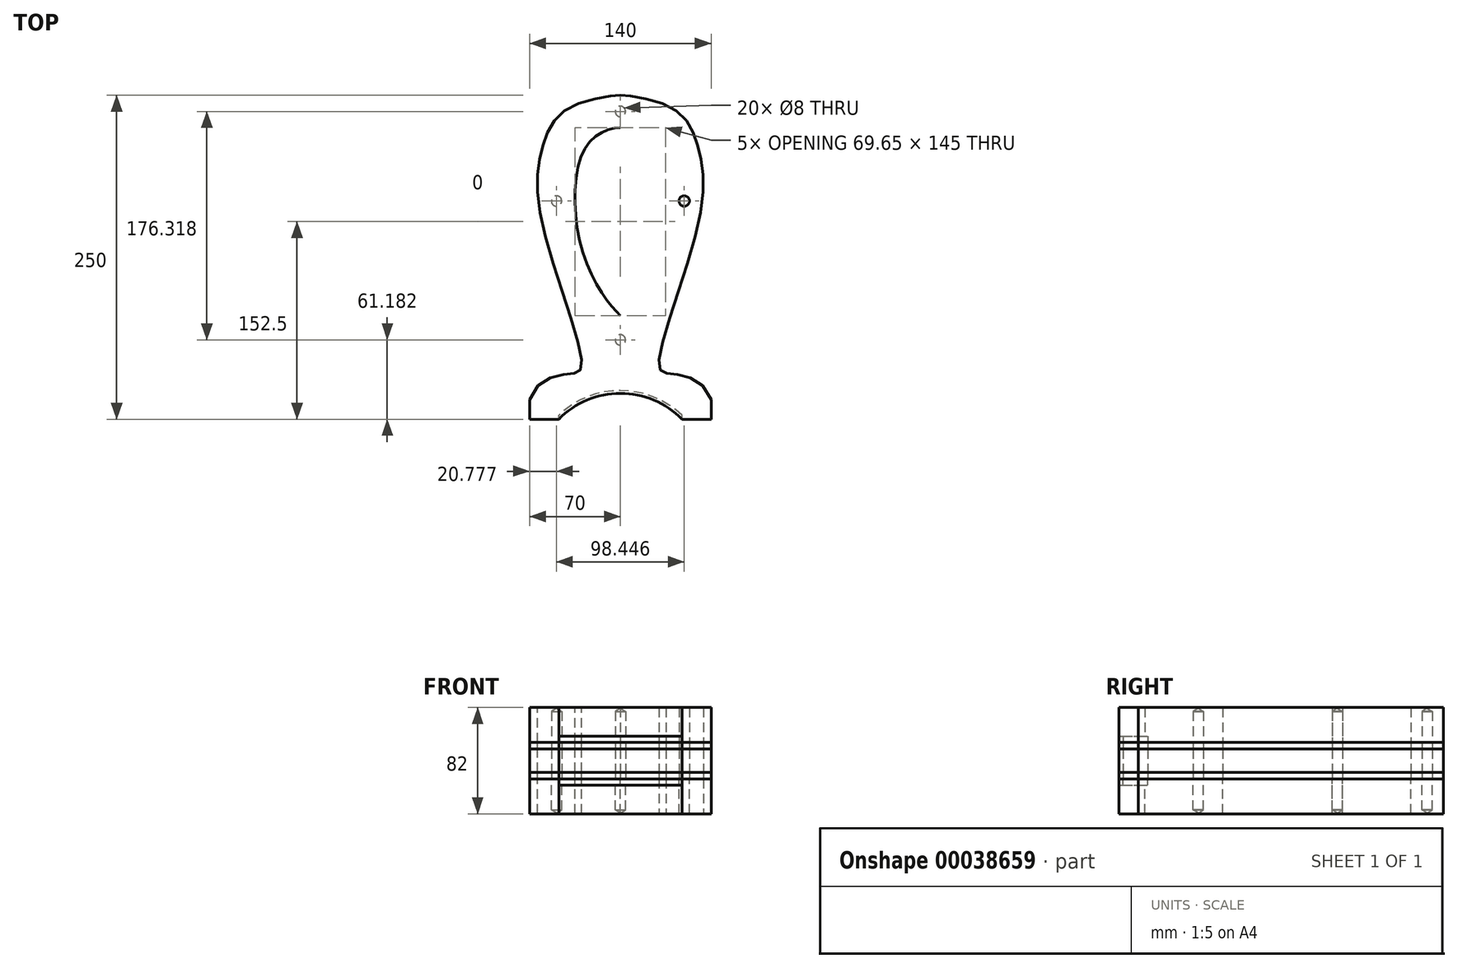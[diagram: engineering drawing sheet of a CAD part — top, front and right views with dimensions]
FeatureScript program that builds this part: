
annotation { "Feature Type Name" : "Feature", "Feature Type Description" : "" }
export const myFeature = defineFeature(function(context is Context, id is Id, definition is map)
    precondition{}
    {
        {
            assignVariable(context, id + "F0", {"name" : "WoodFrontWidth", "anyValue" : 27});
        }
        {
            assignVariable(context, id + "F1", {"name" : "WoodMiddleWidth", "anyValue" : 18});
        }
        {
            assignVariable(context, id + "F2", {"name" : "PlexiWidth", "anyValue" : 5});
        }
        {
            var Q0;
            Q0=qCreatedBy(makeId("Top.planeOp"),FACE);
            var sketch = newSketch(context, id + "F3", { "sketchPlane" : qUnion([Q0])});
            skLineSegment(sketch, "E0", {"start": v(-70, -35) * mm, "end": v(-47.5, -35) * mm});
            skArc(sketch, "E1", {"start": v(0, -15) * mm, "mid": v(-25.77, -20.2) * mm, "end": v(-47.5, -35) * mm});
            skLineSegment(sketch, "E2", {"start": v(-70, -35) * mm, "end": v(-70, -20) * mm});
            skFitSpline(sketch, "E3", {"points": [v(-70, -20) * mm, v(-40, 0) * mm, v(-30, 5) * mm, v(-60, 115) * mm, v(-60, 175) * mm, v(-40, 205) * mm, v(0, 215) * mm], "startDerivative": vector(94.53, 318.3) * mm, "endDerivative": vector(113.11, -0.2) * mm});
            skFitSpline(sketch, "E4", {"points": [v(0, 190) * mm, v(-26.56, 175) * mm, v(-27.76, 90.21) * mm, v(0, 45) * mm], "startDerivative": vector(-99.5, -1.22) * mm, "endDerivative": vector(63.74, -58) * mm});
            skArc(sketch, "E5.MirrorCS", {"start": v(0, -15) * mm, "mid": v(25.77, -20.2) * mm, "end": v(47.5, -35) * mm});
            skLineSegment(sketch, "E6.MirrorCS", {"start": v(70, -35) * mm, "end": v(70, -20) * mm});
            skLineSegment(sketch, "E7.MirrorCS", {"start": v(70, -35) * mm, "end": v(47.5, -35) * mm});
            skFitSpline(sketch, "E8.MirrorCS", {"points": [v(70, -20) * mm, v(40, 0) * mm, v(30, 5) * mm, v(60, 115) * mm, v(60, 175) * mm, v(40, 205) * mm, v(0, 215) * mm], "startDerivative": vector(-94.53, 318.3) * mm, "endDerivative": vector(-113.11, -0.2) * mm});
            skFitSpline(sketch, "E9.MirrorCS", {"points": [v(-70, -20) * mm, v(-40, 0) * mm, v(-30, 5) * mm, v(-60, 115) * mm, v(-60, 175) * mm, v(-40, 205) * mm, v(0, 215) * mm], "startDerivative": vector(94.53, 318.3) * mm, "endDerivative": vector(113.11, -0.2) * mm});
            skFitSpline(sketch, "E10.MirrorCS", {"points": [v(70, -20) * mm, v(40, 0) * mm, v(30, 5) * mm, v(60, 115) * mm, v(60, 175) * mm, v(40, 205) * mm, v(0, 215) * mm], "startDerivative": vector(-94.53, 318.3) * mm, "endDerivative": vector(-113.11, -0.2) * mm});
            skFitSpline(sketch, "E11.MirrorCS", {"points": [v(0, 190) * mm, v(26.56, 175) * mm, v(27.76, 90.21) * mm, v(0, 45) * mm], "startDerivative": vector(99.5, -1.22) * mm, "endDerivative": vector(-63.74, -58) * mm});
            skCircle(sketch, "E12", {"center": v(0, 26.18) * mm, "radius": 4 * mm});
            skCircle(sketch, "E13", {"center": v(-49.22, 133.37) * mm, "radius": 4 * mm});
            skCircle(sketch, "E14", {"center": v(0, 202.5) * mm, "radius": 4 * mm});
            skCircle(sketch, "E15.MirrorC", {"center": v(49.22, 133.37) * mm, "radius": 4 * mm});
            skLineSegment(sketch, "E16.bottom", {"start": v(-37, -26.26) * mm, "end": v(37, -26.26) * mm});
            skLineSegment(sketch, "E16.top", {"start": v(-37, -56.26) * mm, "end": v(37, -56.26) * mm});
            skLineSegment(sketch, "E16.left", {"start": v(-37, -26.26) * mm, "end": v(-37, -56.26) * mm});
            skLineSegment(sketch, "E16.right", {"start": v(37, -26.26) * mm, "end": v(37, -56.26) * mm});
            skLineSegment(sketch, "E17.bottom", {"start": v(-47.5, -56.26) * mm, "end": v(47.5, -56.26) * mm});
            skLineSegment(sketch, "E17.top", {"start": v(-47.5, -88.26) * mm, "end": v(47.5, -88.26) * mm});
            skLineSegment(sketch, "E17.left", {"start": v(-47.5, -56.26) * mm, "end": v(-47.5, -88.26) * mm});
            skLineSegment(sketch, "E17.right", {"start": v(47.5, -56.26) * mm, "end": v(47.5, -88.26) * mm});
            skLineSegment(sketch, "E18", {"start": v(-47.5, -88.26) * mm, "end": v(-70, -88.26) * mm});
            skLineSegment(sketch, "E19", {"start": v(-70, -88.26) * mm, "end": v(-70, -35) * mm});
            skLineSegment(sketch, "E20.MirrorCS", {"start": v(70, -88.26) * mm, "end": v(70, -35) * mm});
            skLineSegment(sketch, "E21.MirrorCS", {"start": v(47.5, -88.26) * mm, "end": v(70, -88.26) * mm});
            skLineSegment(sketch, "E22", {"start": v(-47.5, -35) * mm, "end": v(-47.5, -32) * mm});
            skArc(sketch, "E23", {"start": v(0, -12.87) * mm, "mid": v(-25.6, -17.83) * mm, "end": v(-47.5, -32) * mm});
            skArc(sketch, "E24.MirrorCS", {"start": v(0, -12.87) * mm, "mid": v(25.6, -17.83) * mm, "end": v(47.5, -32) * mm});
            skLineSegment(sketch, "E25.MirrorCS", {"start": v(47.5, -35) * mm, "end": v(47.5, -32) * mm});
            skSolve(sketch);
        }
        {
            var Q0;
            Q0=makeQuery(id+"F3.imprint","IMPRINT",FACE,{"disambiguationData":[TD([[makeQuery(id+"F3.imprint","IMPRINT",EDGE,{"derivedFrom":sQuery(id+"F3.wireOp",EDGE,"E0")}),1.0]])]});
            var Q1;
            Q1=makeQuery(id+"F3.imprint","IMPRINT",FACE,{"disambiguationData":[TD([[makeQuery(id+"F3.imprint","IMPRINT",EDGE,{"derivedFrom":sQuery(id+"F3.wireOp",EDGE,"E14")}),1.0]])]});
            var Q2;
            Q2=makeQuery(id+"F3.imprint","IMPRINT",FACE,{"disambiguationData":[TD([[makeQuery(id+"F3.imprint","IMPRINT",EDGE,{"derivedFrom":sQuery(id+"F3.wireOp",EDGE,"E15.MirrorC")}),-1.0]])]});
            var Q3;
            Q3=makeQuery(id+"F3.imprint","IMPRINT",FACE,{"disambiguationData":[TD([[makeQuery(id+"F3.imprint","IMPRINT",EDGE,{"derivedFrom":sQuery(id+"F3.wireOp",EDGE,"E12")}),1.0]])]});
            var Q4;
            Q4=makeQuery(id+"F3.imprint","IMPRINT",FACE,{"disambiguationData":[TD([[makeQuery(id+"F3.imprint","IMPRINT",EDGE,{"derivedFrom":sQuery(id+"F3.wireOp",EDGE,"E13")}),1.0]])]});
            var Q5;
            {var subQ6=sQuery(id+"F3.wireOp",EDGE,"E22");Q5=makeQuery(id+"F3.imprint","IMPRINT",FACE,{"disambiguationData":[TD([[makeQuery(id+"F3.imprint","IMPRINT",EDGE,{"derivedFrom":subQ6}),-1.0]])]});}
            extrude(context, id + "F4", {"entities" : qUnion([Q0, Q1, Q2, Q3, Q4, Q5]), "depth" : (getVariable(context, 'WoodFrontWidth')) * mm});
        }
        {
            var Q0;
            Q0=sQuery(id+"F3.wireOp",VERTEX,"E14.center");
            var Q1;
            Q1=sQuery(id+"F3.wireOp",VERTEX,"E13.center");
            var Q2;
            Q2=sQuery(id+"F3.wireOp",VERTEX,"E12.center");
            var Q3;
            Q3=sQuery(id+"F3.wireOp",VERTEX,"E15.MirrorC.center");
            var Q4;
            Q4=makeQuery(id+"F4.opExtrude","SWEPT_BODY",BODY,{"disambiguationData":[OSD([sQuery(id+"F3.wireOp",EDGE,"E0"),sQuery(id+"F3.wireOp",EDGE,"E1"),sQuery(id+"F3.wireOp",EDGE,"E2"),sQuery(id+"F3.wireOp",EDGE,"E4"),sQuery(id+"F3.wireOp",EDGE,"E5.MirrorCS"),sQuery(id+"F3.wireOp",EDGE,"E6.MirrorCS"),sQuery(id+"F3.wireOp",EDGE,"E7.MirrorCS"),sQuery(id+"F3.wireOp",EDGE,"E9.MirrorCS"),sQuery(id+"F3.wireOp",EDGE,"E10.MirrorCS"),sQuery(id+"F3.wireOp",EDGE,"E11.MirrorCS")])]});
            hole(context, id + "F5", {"style" : HoleStyle.SIMPLE, "holeDiameter" : 8 * mm, "endStyle" : HoleEndStyle.BLIND, "oppositeDirection" : true, "holeDepth" : (getVariable(context, 'WoodFrontWidth') - 3) * mm, "locations" : qUnion([Q0, Q1, Q2, Q3]), "scope" : qUnion([Q4])});
        }
        {
            var Q0;
            {var subQ6=sQuery(id+"F3.wireOp",EDGE,"E22");Q0=makeQuery(id+"F3.imprint","IMPRINT",FACE,{"disambiguationData":[TD([[makeQuery(id+"F3.imprint","IMPRINT",EDGE,{"derivedFrom":subQ6}),-1.0]])]});}
            extrude(context, id + "F6", {"entities" : qUnion([Q0]), "operationType" : NewBodyOperationType.REMOVE, "depth" : 5 * mm});
        }
        {
            var Q0;
            Q0=makeQuery(id+"F4.opExtrude","SWEPT_BODY",BODY,{"disambiguationData":[OSD([sQuery(id+"F3.wireOp",EDGE,"E0"),sQuery(id+"F3.wireOp",EDGE,"E1"),sQuery(id+"F3.wireOp",EDGE,"E2"),sQuery(id+"F3.wireOp",EDGE,"E4"),sQuery(id+"F3.wireOp",EDGE,"E5.MirrorCS"),sQuery(id+"F3.wireOp",EDGE,"E6.MirrorCS"),sQuery(id+"F3.wireOp",EDGE,"E7.MirrorCS"),sQuery(id+"F3.wireOp",EDGE,"E9.MirrorCS"),sQuery(id+"F3.wireOp",EDGE,"E10.MirrorCS"),sQuery(id+"F3.wireOp",EDGE,"E11.MirrorCS")])]});
            transform(context, id + "F7", {"entities" : qUnion([Q0]), "transformType" : TransformType.TRANSLATION_3D, "dx" : 0 * mm, "dy" : 0 * mm, "dz" : -(2 * getVariable(context, 'WoodFrontWidth') + getVariable(context, 'WoodMiddleWidth') + 2 * getVariable(context, 'PlexiWidth')) * mm, "makeCopy" : true});
        }
        {
            var Q0;
            Q0=makeQuery(id+"F7.opPattern","COPY",BODY,{"derivedFrom":makeQuery(id+"F4.opExtrude","SWEPT_BODY",BODY,{"disambiguationData":[OSD([sQuery(id+"F3.wireOp",EDGE,"E0"),sQuery(id+"F3.wireOp",EDGE,"E1"),sQuery(id+"F3.wireOp",EDGE,"E2"),sQuery(id+"F3.wireOp",EDGE,"E4"),sQuery(id+"F3.wireOp",EDGE,"E5.MirrorCS"),sQuery(id+"F3.wireOp",EDGE,"E6.MirrorCS"),sQuery(id+"F3.wireOp",EDGE,"E7.MirrorCS"),sQuery(id+"F3.wireOp",EDGE,"E9.MirrorCS"),sQuery(id+"F3.wireOp",EDGE,"E10.MirrorCS"),sQuery(id+"F3.wireOp",EDGE,"E11.MirrorCS")])]}),"instanceName":"1"});
            var Q1;
            Q1=makeQuery(id+"F7.opPattern","COPY",FACE,{"derivedFrom":makeQuery(id+"F4.opExtrude","CAP_FACE",FACE,{"disambiguationData":[OSD([sQuery(id+"F3.wireOp",EDGE,"E0"),sQuery(id+"F3.wireOp",EDGE,"E1"),sQuery(id+"F3.wireOp",EDGE,"E2"),sQuery(id+"F3.wireOp",EDGE,"E4"),sQuery(id+"F3.wireOp",EDGE,"E5.MirrorCS"),sQuery(id+"F3.wireOp",EDGE,"E6.MirrorCS"),sQuery(id+"F3.wireOp",EDGE,"E7.MirrorCS"),sQuery(id+"F3.wireOp",EDGE,"E9.MirrorCS"),sQuery(id+"F3.wireOp",EDGE,"E10.MirrorCS"),sQuery(id+"F3.wireOp",EDGE,"E11.MirrorCS")])],"isStart":false}),"instanceName":"1"});
            mirror(context, id + "F8", {"entities" : qUnion([Q0]), "mirrorPlane" : qUnion([Q1])});
        }
        {
            var Q0;
            Q0=makeQuery(id+"F7.opPattern","COPY",BODY,{"derivedFrom":makeQuery(id+"F4.opExtrude","SWEPT_BODY",BODY,{"disambiguationData":[OSD([sQuery(id+"F3.wireOp",EDGE,"E0"),sQuery(id+"F3.wireOp",EDGE,"E1"),sQuery(id+"F3.wireOp",EDGE,"E2"),sQuery(id+"F3.wireOp",EDGE,"E4"),sQuery(id+"F3.wireOp",EDGE,"E5.MirrorCS"),sQuery(id+"F3.wireOp",EDGE,"E6.MirrorCS"),sQuery(id+"F3.wireOp",EDGE,"E7.MirrorCS"),sQuery(id+"F3.wireOp",EDGE,"E9.MirrorCS"),sQuery(id+"F3.wireOp",EDGE,"E10.MirrorCS"),sQuery(id+"F3.wireOp",EDGE,"E11.MirrorCS")])]}),"instanceName":"1"});
            deleteBodies(context, id + "F9", {"entities" : qUnion([Q0])});
        }
        {
            var Q0;
            Q0=makeQuery(id+"F3.imprint","IMPRINT",FACE,{"disambiguationData":[TD([[makeQuery(id+"F3.imprint","IMPRINT",EDGE,{"derivedFrom":sQuery(id+"F3.wireOp",EDGE,"E0")}),1.0]])]});
            extrude(context, id + "F10", {"entities" : qUnion([Q0]), "depth" : (getVariable(context, 'PlexiWidth')) * mm});
        }
        {
            var Q0;
            Q0=makeQuery(id+"F10.opExtrude","SWEPT_BODY",BODY,{"disambiguationData":[OSD([sQuery(id+"F3.wireOp",EDGE,"E0"),sQuery(id+"F3.wireOp",EDGE,"E2"),sQuery(id+"F3.wireOp",EDGE,"E4"),sQuery(id+"F3.wireOp",EDGE,"E6.MirrorCS"),sQuery(id+"F3.wireOp",EDGE,"E7.MirrorCS"),sQuery(id+"F3.wireOp",EDGE,"E9.MirrorCS"),sQuery(id+"F3.wireOp",EDGE,"E10.MirrorCS"),sQuery(id+"F3.wireOp",EDGE,"E11.MirrorCS"),sQuery(id+"F3.wireOp",EDGE,"E12"),sQuery(id+"F3.wireOp",EDGE,"E13"),sQuery(id+"F3.wireOp",EDGE,"E14"),sQuery(id+"F3.wireOp",EDGE,"E15.MirrorC"),sQuery(id+"F3.wireOp",EDGE,"E22"),sQuery(id+"F3.wireOp",EDGE,"E23"),sQuery(id+"F3.wireOp",EDGE,"E24.MirrorCS"),sQuery(id+"F3.wireOp",EDGE,"E25.MirrorCS")])]});
            transform(context, id + "F11", {"entities" : qUnion([Q0]), "transformType" : TransformType.TRANSLATION_3D, "dx" : 0 * mm, "dy" : 0 * mm, "dz" : (-getVariable(context, 'PlexiWidth')) * mm, "makeCopy" : false});
        }
        {
            var Q0;
            Q0=makeQuery(id+"F3.imprint","IMPRINT",FACE,{"disambiguationData":[TD([[makeQuery(id+"F3.imprint","IMPRINT",EDGE,{"derivedFrom":sQuery(id+"F3.wireOp",EDGE,"E0")}),1.0]])]});
            extrude(context, id + "F12", {"entities" : qUnion([Q0]), "depth" : (getVariable(context, 'PlexiWidth')) * mm});
        }
        {
            var Q0;
            Q0=makeQuery(id+"F3.imprint","IMPRINT",FACE,{"disambiguationData":[TD([[makeQuery(id+"F3.imprint","IMPRINT",EDGE,{"derivedFrom":sQuery(id+"F3.wireOp",EDGE,"E0")}),1.0]])]});
            extrude(context, id + "F13", {"entities" : qUnion([Q0]), "depth" : (getVariable(context, 'WoodMiddleWidth')) * mm});
        }
        {
            var Q0;
            Q0=makeQuery(id+"F13.opExtrude","SWEPT_BODY",BODY,{"disambiguationData":[OSD([sQuery(id+"F3.wireOp",EDGE,"E0"),sQuery(id+"F3.wireOp",EDGE,"E2"),sQuery(id+"F3.wireOp",EDGE,"E4"),sQuery(id+"F3.wireOp",EDGE,"E6.MirrorCS"),sQuery(id+"F3.wireOp",EDGE,"E7.MirrorCS"),sQuery(id+"F3.wireOp",EDGE,"E9.MirrorCS"),sQuery(id+"F3.wireOp",EDGE,"E10.MirrorCS"),sQuery(id+"F3.wireOp",EDGE,"E11.MirrorCS"),sQuery(id+"F3.wireOp",EDGE,"E12"),sQuery(id+"F3.wireOp",EDGE,"E13"),sQuery(id+"F3.wireOp",EDGE,"E14"),sQuery(id+"F3.wireOp",EDGE,"E15.MirrorC"),sQuery(id+"F3.wireOp",EDGE,"E22"),sQuery(id+"F3.wireOp",EDGE,"E23"),sQuery(id+"F3.wireOp",EDGE,"E24.MirrorCS"),sQuery(id+"F3.wireOp",EDGE,"E25.MirrorCS")])]});
            transform(context, id + "F14", {"entities" : qUnion([Q0]), "transformType" : TransformType.TRANSLATION_3D, "dx" : 0 * mm, "dy" : 0 * mm, "dz" : (-(getVariable(context, 'WoodMiddleWidth') + getVariable(context, 'PlexiWidth'))) * mm, "makeCopy" : false});
        }
        {
            var Q0;
            Q0=makeQuery(id+"F12.opExtrude","SWEPT_BODY",BODY,{"disambiguationData":[OSD([sQuery(id+"F3.wireOp",EDGE,"E0"),sQuery(id+"F3.wireOp",EDGE,"E2"),sQuery(id+"F3.wireOp",EDGE,"E4"),sQuery(id+"F3.wireOp",EDGE,"E6.MirrorCS"),sQuery(id+"F3.wireOp",EDGE,"E7.MirrorCS"),sQuery(id+"F3.wireOp",EDGE,"E9.MirrorCS"),sQuery(id+"F3.wireOp",EDGE,"E10.MirrorCS"),sQuery(id+"F3.wireOp",EDGE,"E11.MirrorCS"),sQuery(id+"F3.wireOp",EDGE,"E12"),sQuery(id+"F3.wireOp",EDGE,"E13"),sQuery(id+"F3.wireOp",EDGE,"E14"),sQuery(id+"F3.wireOp",EDGE,"E15.MirrorC"),sQuery(id+"F3.wireOp",EDGE,"E22"),sQuery(id+"F3.wireOp",EDGE,"E23"),sQuery(id+"F3.wireOp",EDGE,"E24.MirrorCS"),sQuery(id+"F3.wireOp",EDGE,"E25.MirrorCS")])]});
            transform(context, id + "F15", {"entities" : qUnion([Q0]), "transformType" : TransformType.TRANSLATION_3D, "dx" : 0 * mm, "dy" : 0 * mm, "dz" : (-(getVariable(context, 'WoodMiddleWidth') + 2 * getVariable(context, 'PlexiWidth'))) * mm, "makeCopy" : false});
        }
    });
